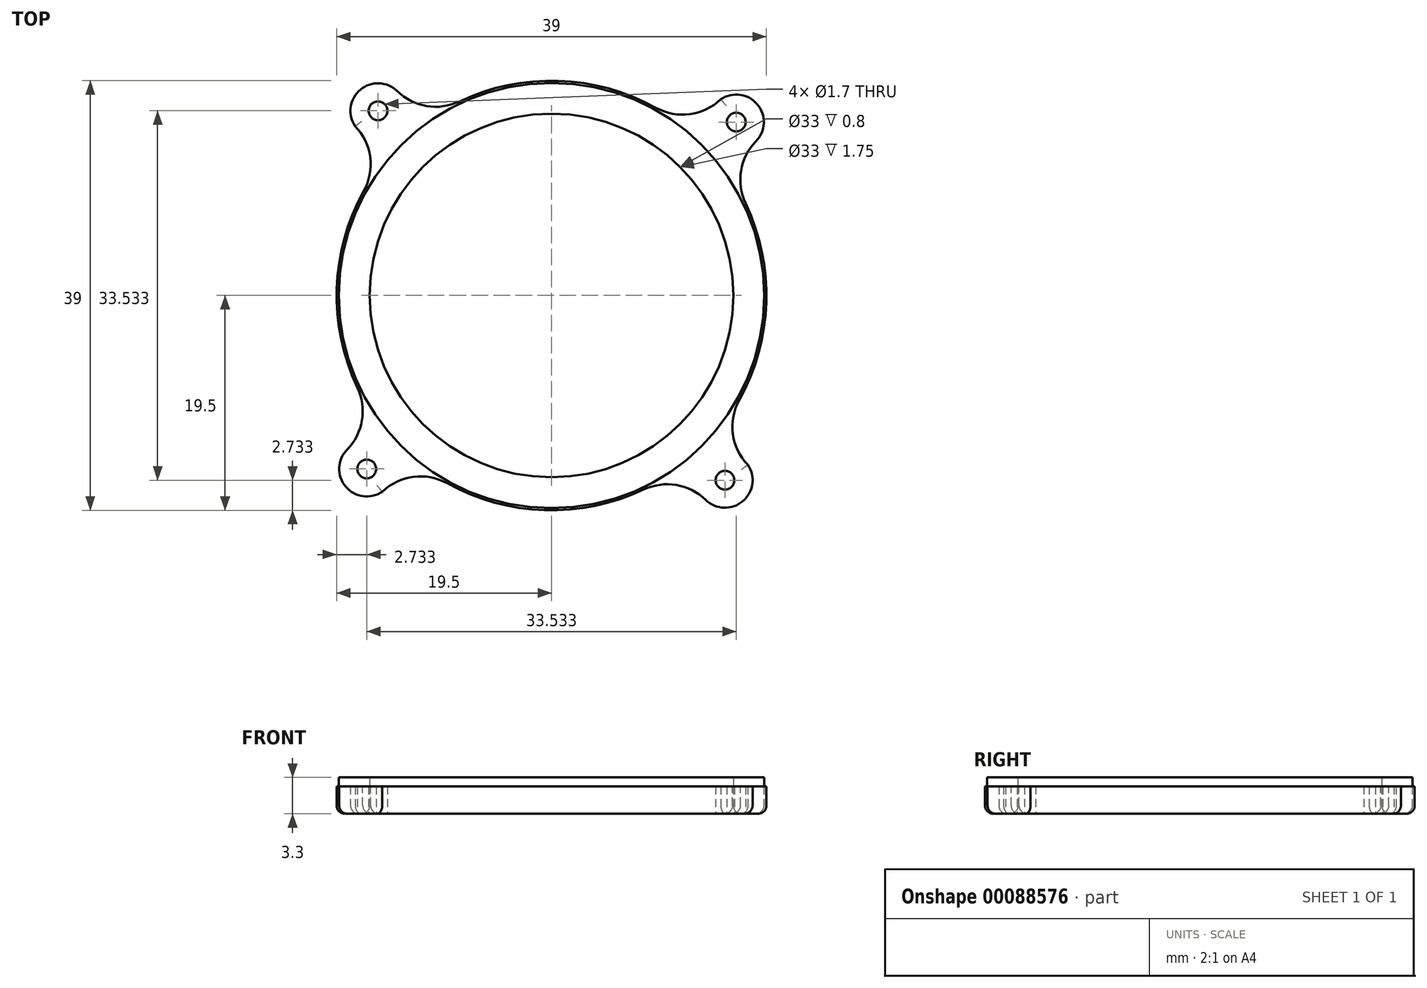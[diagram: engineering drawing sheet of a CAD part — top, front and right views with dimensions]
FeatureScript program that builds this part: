
annotation { "Feature Type Name" : "Feature", "Feature Type Description" : "" }
export const myFeature = defineFeature(function(context is Context, id is Id, definition is map)
    precondition{}
    {
        {
            var Q0;
            Q0=qCreatedBy(makeId("Top.planeOp"),FACE);
            var sketch = newSketch(context, id + "F0", { "sketchPlane" : qUnion([Q0])});
            skCircle(sketch, "E0", {"center": v(0, 0) * mm, "radius": 19.5 * mm});
            skCircle(sketch, "E1", {"center": v(0, 0) * mm, "radius": 16.5 * mm});
            skCircle(sketch, "E2", {"center": v(16.77, 15.74) * mm, "radius": 0.85 * mm});
            skCircle(sketch, "E3.1.0", {"center": v(-15.74, 16.77) * mm, "radius": 0.85 * mm});
            skCircle(sketch, "E3.2.0", {"center": v(-16.77, -15.74) * mm, "radius": 0.85 * mm});
            skCircle(sketch, "E3.3.0", {"center": v(15.74, -16.77) * mm, "radius": 0.85 * mm});
            skCircle(sketch, "E4", {"center": v(-15.74, 16.77) * mm, "radius": 2.5 * mm});
            skLineSegment(sketch, "E5", {"start": v(-13.87, 18.42) * mm, "end": v(-11.5, 15.75) * mm});
            skLineSegment(sketch, "E6", {"start": v(-17.81, 15.36) * mm, "end": v(-14.8, 12.7) * mm});
            skLineSegment(sketch, "E7.1.0", {"start": v(-18.42, -13.87) * mm, "end": v(-15.75, -11.5) * mm});
            skLineSegment(sketch, "E7.1.1", {"start": v(-15.36, -17.81) * mm, "end": v(-12.7, -14.8) * mm});
            skCircle(sketch, "E7.1.2", {"center": v(-16.77, -15.74) * mm, "radius": 2.5 * mm});
            skLineSegment(sketch, "E7.2.0", {"start": v(13.87, -18.42) * mm, "end": v(11.5, -15.75) * mm});
            skLineSegment(sketch, "E7.2.1", {"start": v(17.81, -15.36) * mm, "end": v(14.8, -12.7) * mm});
            skCircle(sketch, "E7.2.2", {"center": v(15.74, -16.77) * mm, "radius": 2.5 * mm});
            skLineSegment(sketch, "E7.3.0", {"start": v(18.42, 13.87) * mm, "end": v(15.75, 11.5) * mm});
            skLineSegment(sketch, "E7.3.1", {"start": v(15.36, 17.81) * mm, "end": v(12.7, 14.8) * mm});
            skCircle(sketch, "E7.3.2", {"center": v(16.77, 15.74) * mm, "radius": 2.5 * mm});
            skSolve(sketch);
        }
        {
            var Q0;
            Q0=makeQuery(id+"F0.imprint","IMPRINT",FACE,{"disambiguationData":[TD([[makeQuery(id+"F0.imprint","IMPRINT",EDGE,{"derivedFrom":sQuery(id+"F0.wireOp",EDGE,"E2")}),-1.0]])]});
            var Q1;
            {var subQ0=sQuery(id+"F0.wireOp",EDGE,"E7.3.0");Q1=makeQuery(id+"F0.imprint","IMPRINT",FACE,{"disambiguationData":[TD([[makeQuery(id+"F0.imprint","IMPRINT",EDGE,{"derivedFrom":subQ0}),-1.0]])]});}
            var Q2;
            Q2=makeQuery(id+"F0.imprint","IMPRINT",FACE,{"disambiguationData":[TD([[makeQuery(id+"F0.imprint","IMPRINT",EDGE,{"derivedFrom":sQuery(id+"F0.wireOp",EDGE,"E3.1.0")}),-1.0]])]});
            var Q3;
            {var subQ0=sQuery(id+"F0.wireOp",EDGE,"E5");Q3=makeQuery(id+"F0.imprint","IMPRINT",FACE,{"disambiguationData":[TD([[makeQuery(id+"F0.imprint","IMPRINT",EDGE,{"derivedFrom":subQ0}),-1.0]])]});}
            var Q4;
            Q4=makeQuery(id+"F0.imprint","IMPRINT",FACE,{"disambiguationData":[TD([[makeQuery(id+"F0.imprint","IMPRINT",EDGE,{"derivedFrom":sQuery(id+"F0.wireOp",EDGE,"E1")}),-1.0]])]});
            var Q5;
            {var subQ0=sQuery(id+"F0.wireOp",EDGE,"E7.2.0");Q5=makeQuery(id+"F0.imprint","IMPRINT",FACE,{"disambiguationData":[TD([[makeQuery(id+"F0.imprint","IMPRINT",EDGE,{"derivedFrom":subQ0}),-1.0]])]});}
            var Q6;
            {var subQ0=sQuery(id+"F0.wireOp",EDGE,"E7.1.0");Q6=makeQuery(id+"F0.imprint","IMPRINT",FACE,{"disambiguationData":[TD([[makeQuery(id+"F0.imprint","IMPRINT",EDGE,{"derivedFrom":subQ0}),-1.0]])]});}
            var Q7;
            Q7=makeQuery(id+"F0.imprint","IMPRINT",FACE,{"disambiguationData":[TD([[makeQuery(id+"F0.imprint","IMPRINT",EDGE,{"derivedFrom":sQuery(id+"F0.wireOp",EDGE,"E3.2.0")}),-1.0]])]});
            var Q8;
            Q8=makeQuery(id+"F0.imprint","IMPRINT",FACE,{"disambiguationData":[TD([[makeQuery(id+"F0.imprint","IMPRINT",EDGE,{"derivedFrom":sQuery(id+"F0.wireOp",EDGE,"E3.3.0")}),-1.0]])]});
            extrude(context, id + "F1", {"entities" : qUnion([Q0, Q1, Q2, Q3, Q4, Q5, Q6, Q7, Q8]), "depth" : 2.5 * mm});
        }
        {
            var Q0;
            Q0=makeQuery(id+"F1.opExtrude","SWEPT_EDGE",EDGE,{"disambiguationData":[OSD([sQuery(id+"F0.wireOp",EDGE,"E0"),sQuery(id+"F0.wireOp",EDGE,"E7.3.0")])]});
            var Q1;
            Q1=makeQuery(id+"F1.opExtrude","SWEPT_EDGE",EDGE,{"disambiguationData":[OSD([sQuery(id+"F0.wireOp",EDGE,"E0"),sQuery(id+"F0.wireOp",EDGE,"E7.3.1")])]});
            var Q2;
            Q2=makeQuery(id+"F1.opExtrude","SWEPT_EDGE",EDGE,{"disambiguationData":[OSD([sQuery(id+"F0.wireOp",EDGE,"E0"),sQuery(id+"F0.wireOp",EDGE,"E5")])]});
            var Q3;
            Q3=makeQuery(id+"F1.opExtrude","SWEPT_EDGE",EDGE,{"disambiguationData":[OSD([sQuery(id+"F0.wireOp",EDGE,"E0"),sQuery(id+"F0.wireOp",EDGE,"E6")])]});
            var Q4;
            Q4=makeQuery(id+"F1.opExtrude","SWEPT_EDGE",EDGE,{"disambiguationData":[OSD([sQuery(id+"F0.wireOp",EDGE,"E0"),sQuery(id+"F0.wireOp",EDGE,"E7.1.0")])]});
            var Q5;
            Q5=makeQuery(id+"F1.opExtrude","SWEPT_EDGE",EDGE,{"disambiguationData":[OSD([sQuery(id+"F0.wireOp",EDGE,"E0"),sQuery(id+"F0.wireOp",EDGE,"E7.1.1")])]});
            var Q6;
            Q6=makeQuery(id+"F1.opExtrude","SWEPT_EDGE",EDGE,{"disambiguationData":[OSD([sQuery(id+"F0.wireOp",EDGE,"E0"),sQuery(id+"F0.wireOp",EDGE,"E7.2.0")])]});
            var Q7;
            Q7=makeQuery(id+"F1.opExtrude","SWEPT_EDGE",EDGE,{"disambiguationData":[OSD([sQuery(id+"F0.wireOp",EDGE,"E0"),sQuery(id+"F0.wireOp",EDGE,"E7.2.1")])]});
            fillet(context, id + "F2", {"entities" : qUnion([Q0, Q1, Q2, Q3, Q4, Q5, Q6, Q7]), "radius" : 5 * mm, "tangentPropagation" : true, "allowEdgeOverflow" : false});
        }
        {
            var Q0;
            {var subQ0=sQuery(id+"F0.wireOp",EDGE,"E0");Q0=makeQuery(id+"F1.opExtrude","CAP_EDGE",EDGE,{"disambiguationData":[OSD([subQ0]),TDD([makeQuery(id+"F0.imprint","IMPRINT",EDGE,{"disambiguationData":[TD([[makeQuery(id+"F0.imprint","INTERSECT",VERTEX,{"derivedFrom":[subQ0,sQuery(id+"F0.wireOp",EDGE,"E6")]}),-1.0]])],"derivedFrom":subQ0})])],"isStart":true});}
            var Q1;
            {var subQ0=sQuery(id+"F0.wireOp",EDGE,"E6");var subQ1=sQuery(id+"F0.wireOp",EDGE,"E0");Q1=makeQuery(id+"F2.opFillet","BLEND_EDGE",EDGE,{"blendedFrom":[makeQuery(id+"F1.opExtrude","SWEPT_EDGE",EDGE,{"disambiguationData":[OSD([subQ1,subQ0])]}),makeQuery(id+"F1.opExtrude","CAP_FACE",FACE,{"disambiguationData":[OSD([subQ1,sQuery(id+"F0.wireOp",EDGE,"E1"),sQuery(id+"F0.wireOp",EDGE,"E2"),sQuery(id+"F0.wireOp",EDGE,"E3.1.0"),sQuery(id+"F0.wireOp",EDGE,"E3.2.0"),sQuery(id+"F0.wireOp",EDGE,"E3.3.0"),sQuery(id+"F0.wireOp",EDGE,"E4"),sQuery(id+"F0.wireOp",EDGE,"E5"),subQ0,sQuery(id+"F0.wireOp",EDGE,"E7.1.0"),sQuery(id+"F0.wireOp",EDGE,"E7.1.1"),sQuery(id+"F0.wireOp",EDGE,"E7.1.2"),sQuery(id+"F0.wireOp",EDGE,"E7.2.0"),sQuery(id+"F0.wireOp",EDGE,"E7.2.1"),sQuery(id+"F0.wireOp",EDGE,"E7.2.2"),sQuery(id+"F0.wireOp",EDGE,"E7.3.0"),sQuery(id+"F0.wireOp",EDGE,"E7.3.1"),sQuery(id+"F0.wireOp",EDGE,"E7.3.2")])],"isStart":true})],"blendedInto":[makeQuery(id+"F1.opExtrude","CAP_FACE",FACE,{"disambiguationData":[OSD([subQ1,sQuery(id+"F0.wireOp",EDGE,"E1"),sQuery(id+"F0.wireOp",EDGE,"E2"),sQuery(id+"F0.wireOp",EDGE,"E3.1.0"),sQuery(id+"F0.wireOp",EDGE,"E3.2.0"),sQuery(id+"F0.wireOp",EDGE,"E3.3.0"),sQuery(id+"F0.wireOp",EDGE,"E4"),sQuery(id+"F0.wireOp",EDGE,"E5"),subQ0,sQuery(id+"F0.wireOp",EDGE,"E7.1.0"),sQuery(id+"F0.wireOp",EDGE,"E7.1.1"),sQuery(id+"F0.wireOp",EDGE,"E7.1.2"),sQuery(id+"F0.wireOp",EDGE,"E7.2.0"),sQuery(id+"F0.wireOp",EDGE,"E7.2.1"),sQuery(id+"F0.wireOp",EDGE,"E7.2.2"),sQuery(id+"F0.wireOp",EDGE,"E7.3.0"),sQuery(id+"F0.wireOp",EDGE,"E7.3.1"),sQuery(id+"F0.wireOp",EDGE,"E7.3.2")])],"isStart":true})]});}
            var Q2;
            Q2=makeQuery(id+"F1.opExtrude","CAP_EDGE",EDGE,{"disambiguationData":[OSD([sQuery(id+"F0.wireOp",EDGE,"E4")])],"isStart":true});
            var Q3;
            {var subQ0=sQuery(id+"F0.wireOp",EDGE,"E5");var subQ1=sQuery(id+"F0.wireOp",EDGE,"E0");Q3=makeQuery(id+"F2.opFillet","BLEND_EDGE",EDGE,{"blendedFrom":[makeQuery(id+"F1.opExtrude","SWEPT_EDGE",EDGE,{"disambiguationData":[OSD([subQ1,subQ0])]}),makeQuery(id+"F1.opExtrude","CAP_FACE",FACE,{"disambiguationData":[OSD([subQ1,sQuery(id+"F0.wireOp",EDGE,"E1"),sQuery(id+"F0.wireOp",EDGE,"E2"),sQuery(id+"F0.wireOp",EDGE,"E3.1.0"),sQuery(id+"F0.wireOp",EDGE,"E3.2.0"),sQuery(id+"F0.wireOp",EDGE,"E3.3.0"),sQuery(id+"F0.wireOp",EDGE,"E4"),subQ0,sQuery(id+"F0.wireOp",EDGE,"E6"),sQuery(id+"F0.wireOp",EDGE,"E7.1.0"),sQuery(id+"F0.wireOp",EDGE,"E7.1.1"),sQuery(id+"F0.wireOp",EDGE,"E7.1.2"),sQuery(id+"F0.wireOp",EDGE,"E7.2.0"),sQuery(id+"F0.wireOp",EDGE,"E7.2.1"),sQuery(id+"F0.wireOp",EDGE,"E7.2.2"),sQuery(id+"F0.wireOp",EDGE,"E7.3.0"),sQuery(id+"F0.wireOp",EDGE,"E7.3.1"),sQuery(id+"F0.wireOp",EDGE,"E7.3.2")])],"isStart":true})],"blendedInto":[makeQuery(id+"F1.opExtrude","CAP_FACE",FACE,{"disambiguationData":[OSD([subQ1,sQuery(id+"F0.wireOp",EDGE,"E1"),sQuery(id+"F0.wireOp",EDGE,"E2"),sQuery(id+"F0.wireOp",EDGE,"E3.1.0"),sQuery(id+"F0.wireOp",EDGE,"E3.2.0"),sQuery(id+"F0.wireOp",EDGE,"E3.3.0"),sQuery(id+"F0.wireOp",EDGE,"E4"),subQ0,sQuery(id+"F0.wireOp",EDGE,"E6"),sQuery(id+"F0.wireOp",EDGE,"E7.1.0"),sQuery(id+"F0.wireOp",EDGE,"E7.1.1"),sQuery(id+"F0.wireOp",EDGE,"E7.1.2"),sQuery(id+"F0.wireOp",EDGE,"E7.2.0"),sQuery(id+"F0.wireOp",EDGE,"E7.2.1"),sQuery(id+"F0.wireOp",EDGE,"E7.2.2"),sQuery(id+"F0.wireOp",EDGE,"E7.3.0"),sQuery(id+"F0.wireOp",EDGE,"E7.3.1"),sQuery(id+"F0.wireOp",EDGE,"E7.3.2")])],"isStart":true})]});}
            var Q4;
            {var subQ0=sQuery(id+"F0.wireOp",EDGE,"E0");Q4=makeQuery(id+"F1.opExtrude","CAP_EDGE",EDGE,{"disambiguationData":[OSD([subQ0]),TDD([makeQuery(id+"F0.imprint","IMPRINT",EDGE,{"disambiguationData":[TD([[makeQuery(id+"F0.imprint","INTERSECT",VERTEX,{"derivedFrom":[subQ0,sQuery(id+"F0.wireOp",EDGE,"E5")]}),1.0]])],"derivedFrom":subQ0})])],"isStart":true});}
            var Q5;
            {var subQ0=sQuery(id+"F0.wireOp",EDGE,"E7.3.1");var subQ1=sQuery(id+"F0.wireOp",EDGE,"E0");Q5=makeQuery(id+"F2.opFillet","BLEND_EDGE",EDGE,{"blendedFrom":[makeQuery(id+"F1.opExtrude","SWEPT_EDGE",EDGE,{"disambiguationData":[OSD([subQ1,subQ0])]}),makeQuery(id+"F1.opExtrude","CAP_FACE",FACE,{"disambiguationData":[OSD([subQ1,sQuery(id+"F0.wireOp",EDGE,"E1"),sQuery(id+"F0.wireOp",EDGE,"E2"),sQuery(id+"F0.wireOp",EDGE,"E3.1.0"),sQuery(id+"F0.wireOp",EDGE,"E3.2.0"),sQuery(id+"F0.wireOp",EDGE,"E3.3.0"),sQuery(id+"F0.wireOp",EDGE,"E4"),sQuery(id+"F0.wireOp",EDGE,"E5"),sQuery(id+"F0.wireOp",EDGE,"E6"),sQuery(id+"F0.wireOp",EDGE,"E7.1.0"),sQuery(id+"F0.wireOp",EDGE,"E7.1.1"),sQuery(id+"F0.wireOp",EDGE,"E7.1.2"),sQuery(id+"F0.wireOp",EDGE,"E7.2.0"),sQuery(id+"F0.wireOp",EDGE,"E7.2.1"),sQuery(id+"F0.wireOp",EDGE,"E7.2.2"),sQuery(id+"F0.wireOp",EDGE,"E7.3.0"),subQ0,sQuery(id+"F0.wireOp",EDGE,"E7.3.2")])],"isStart":true})],"blendedInto":[makeQuery(id+"F1.opExtrude","CAP_FACE",FACE,{"disambiguationData":[OSD([subQ1,sQuery(id+"F0.wireOp",EDGE,"E1"),sQuery(id+"F0.wireOp",EDGE,"E2"),sQuery(id+"F0.wireOp",EDGE,"E3.1.0"),sQuery(id+"F0.wireOp",EDGE,"E3.2.0"),sQuery(id+"F0.wireOp",EDGE,"E3.3.0"),sQuery(id+"F0.wireOp",EDGE,"E4"),sQuery(id+"F0.wireOp",EDGE,"E5"),sQuery(id+"F0.wireOp",EDGE,"E6"),sQuery(id+"F0.wireOp",EDGE,"E7.1.0"),sQuery(id+"F0.wireOp",EDGE,"E7.1.1"),sQuery(id+"F0.wireOp",EDGE,"E7.1.2"),sQuery(id+"F0.wireOp",EDGE,"E7.2.0"),sQuery(id+"F0.wireOp",EDGE,"E7.2.1"),sQuery(id+"F0.wireOp",EDGE,"E7.2.2"),sQuery(id+"F0.wireOp",EDGE,"E7.3.0"),subQ0,sQuery(id+"F0.wireOp",EDGE,"E7.3.2")])],"isStart":true})]});}
            var Q6;
            Q6=makeQuery(id+"F1.opExtrude","CAP_EDGE",EDGE,{"disambiguationData":[OSD([sQuery(id+"F0.wireOp",EDGE,"E7.3.2")])],"isStart":true});
            var Q7;
            {var subQ0=sQuery(id+"F0.wireOp",EDGE,"E7.3.0");var subQ1=sQuery(id+"F0.wireOp",EDGE,"E0");Q7=makeQuery(id+"F2.opFillet","BLEND_EDGE",EDGE,{"blendedFrom":[makeQuery(id+"F1.opExtrude","SWEPT_EDGE",EDGE,{"disambiguationData":[OSD([subQ1,subQ0])]}),makeQuery(id+"F1.opExtrude","CAP_FACE",FACE,{"disambiguationData":[OSD([subQ1,sQuery(id+"F0.wireOp",EDGE,"E1"),sQuery(id+"F0.wireOp",EDGE,"E2"),sQuery(id+"F0.wireOp",EDGE,"E3.1.0"),sQuery(id+"F0.wireOp",EDGE,"E3.2.0"),sQuery(id+"F0.wireOp",EDGE,"E3.3.0"),sQuery(id+"F0.wireOp",EDGE,"E4"),sQuery(id+"F0.wireOp",EDGE,"E5"),sQuery(id+"F0.wireOp",EDGE,"E6"),sQuery(id+"F0.wireOp",EDGE,"E7.1.0"),sQuery(id+"F0.wireOp",EDGE,"E7.1.1"),sQuery(id+"F0.wireOp",EDGE,"E7.1.2"),sQuery(id+"F0.wireOp",EDGE,"E7.2.0"),sQuery(id+"F0.wireOp",EDGE,"E7.2.1"),sQuery(id+"F0.wireOp",EDGE,"E7.2.2"),subQ0,sQuery(id+"F0.wireOp",EDGE,"E7.3.1"),sQuery(id+"F0.wireOp",EDGE,"E7.3.2")])],"isStart":true})],"blendedInto":[makeQuery(id+"F1.opExtrude","CAP_FACE",FACE,{"disambiguationData":[OSD([subQ1,sQuery(id+"F0.wireOp",EDGE,"E1"),sQuery(id+"F0.wireOp",EDGE,"E2"),sQuery(id+"F0.wireOp",EDGE,"E3.1.0"),sQuery(id+"F0.wireOp",EDGE,"E3.2.0"),sQuery(id+"F0.wireOp",EDGE,"E3.3.0"),sQuery(id+"F0.wireOp",EDGE,"E4"),sQuery(id+"F0.wireOp",EDGE,"E5"),sQuery(id+"F0.wireOp",EDGE,"E6"),sQuery(id+"F0.wireOp",EDGE,"E7.1.0"),sQuery(id+"F0.wireOp",EDGE,"E7.1.1"),sQuery(id+"F0.wireOp",EDGE,"E7.1.2"),sQuery(id+"F0.wireOp",EDGE,"E7.2.0"),sQuery(id+"F0.wireOp",EDGE,"E7.2.1"),sQuery(id+"F0.wireOp",EDGE,"E7.2.2"),subQ0,sQuery(id+"F0.wireOp",EDGE,"E7.3.1"),sQuery(id+"F0.wireOp",EDGE,"E7.3.2")])],"isStart":true})]});}
            var Q8;
            {var subQ0=sQuery(id+"F0.wireOp",EDGE,"E0");Q8=makeQuery(id+"F1.opExtrude","CAP_EDGE",EDGE,{"disambiguationData":[OSD([subQ0]),TDD([makeQuery(id+"F0.imprint","IMPRINT",EDGE,{"disambiguationData":[TD([[makeQuery(id+"F0.imprint","INTERSECT",VERTEX,{"derivedFrom":[subQ0,sQuery(id+"F0.wireOp",EDGE,"E7.2.1")]}),-1.0]])],"derivedFrom":subQ0})])],"isStart":true});}
            var Q9;
            {var subQ0=sQuery(id+"F0.wireOp",EDGE,"E7.2.1");var subQ1=sQuery(id+"F0.wireOp",EDGE,"E0");Q9=makeQuery(id+"F2.opFillet","BLEND_EDGE",EDGE,{"blendedFrom":[makeQuery(id+"F1.opExtrude","SWEPT_EDGE",EDGE,{"disambiguationData":[OSD([subQ1,subQ0])]}),makeQuery(id+"F1.opExtrude","CAP_FACE",FACE,{"disambiguationData":[OSD([subQ1,sQuery(id+"F0.wireOp",EDGE,"E1"),sQuery(id+"F0.wireOp",EDGE,"E2"),sQuery(id+"F0.wireOp",EDGE,"E3.1.0"),sQuery(id+"F0.wireOp",EDGE,"E3.2.0"),sQuery(id+"F0.wireOp",EDGE,"E3.3.0"),sQuery(id+"F0.wireOp",EDGE,"E4"),sQuery(id+"F0.wireOp",EDGE,"E5"),sQuery(id+"F0.wireOp",EDGE,"E6"),sQuery(id+"F0.wireOp",EDGE,"E7.1.0"),sQuery(id+"F0.wireOp",EDGE,"E7.1.1"),sQuery(id+"F0.wireOp",EDGE,"E7.1.2"),sQuery(id+"F0.wireOp",EDGE,"E7.2.0"),subQ0,sQuery(id+"F0.wireOp",EDGE,"E7.2.2"),sQuery(id+"F0.wireOp",EDGE,"E7.3.0"),sQuery(id+"F0.wireOp",EDGE,"E7.3.1"),sQuery(id+"F0.wireOp",EDGE,"E7.3.2")])],"isStart":true})],"blendedInto":[makeQuery(id+"F1.opExtrude","CAP_FACE",FACE,{"disambiguationData":[OSD([subQ1,sQuery(id+"F0.wireOp",EDGE,"E1"),sQuery(id+"F0.wireOp",EDGE,"E2"),sQuery(id+"F0.wireOp",EDGE,"E3.1.0"),sQuery(id+"F0.wireOp",EDGE,"E3.2.0"),sQuery(id+"F0.wireOp",EDGE,"E3.3.0"),sQuery(id+"F0.wireOp",EDGE,"E4"),sQuery(id+"F0.wireOp",EDGE,"E5"),sQuery(id+"F0.wireOp",EDGE,"E6"),sQuery(id+"F0.wireOp",EDGE,"E7.1.0"),sQuery(id+"F0.wireOp",EDGE,"E7.1.1"),sQuery(id+"F0.wireOp",EDGE,"E7.1.2"),sQuery(id+"F0.wireOp",EDGE,"E7.2.0"),subQ0,sQuery(id+"F0.wireOp",EDGE,"E7.2.2"),sQuery(id+"F0.wireOp",EDGE,"E7.3.0"),sQuery(id+"F0.wireOp",EDGE,"E7.3.1"),sQuery(id+"F0.wireOp",EDGE,"E7.3.2")])],"isStart":true})]});}
            var Q10;
            Q10=makeQuery(id+"F1.opExtrude","CAP_EDGE",EDGE,{"disambiguationData":[OSD([sQuery(id+"F0.wireOp",EDGE,"E7.2.2")])],"isStart":true});
            var Q11;
            {var subQ0=sQuery(id+"F0.wireOp",EDGE,"E7.2.0");var subQ1=sQuery(id+"F0.wireOp",EDGE,"E0");Q11=makeQuery(id+"F2.opFillet","BLEND_EDGE",EDGE,{"blendedFrom":[makeQuery(id+"F1.opExtrude","SWEPT_EDGE",EDGE,{"disambiguationData":[OSD([subQ1,subQ0])]}),makeQuery(id+"F1.opExtrude","CAP_FACE",FACE,{"disambiguationData":[OSD([subQ1,sQuery(id+"F0.wireOp",EDGE,"E1"),sQuery(id+"F0.wireOp",EDGE,"E2"),sQuery(id+"F0.wireOp",EDGE,"E3.1.0"),sQuery(id+"F0.wireOp",EDGE,"E3.2.0"),sQuery(id+"F0.wireOp",EDGE,"E3.3.0"),sQuery(id+"F0.wireOp",EDGE,"E4"),sQuery(id+"F0.wireOp",EDGE,"E5"),sQuery(id+"F0.wireOp",EDGE,"E6"),sQuery(id+"F0.wireOp",EDGE,"E7.1.0"),sQuery(id+"F0.wireOp",EDGE,"E7.1.1"),sQuery(id+"F0.wireOp",EDGE,"E7.1.2"),subQ0,sQuery(id+"F0.wireOp",EDGE,"E7.2.1"),sQuery(id+"F0.wireOp",EDGE,"E7.2.2"),sQuery(id+"F0.wireOp",EDGE,"E7.3.0"),sQuery(id+"F0.wireOp",EDGE,"E7.3.1"),sQuery(id+"F0.wireOp",EDGE,"E7.3.2")])],"isStart":true})],"blendedInto":[makeQuery(id+"F1.opExtrude","CAP_FACE",FACE,{"disambiguationData":[OSD([subQ1,sQuery(id+"F0.wireOp",EDGE,"E1"),sQuery(id+"F0.wireOp",EDGE,"E2"),sQuery(id+"F0.wireOp",EDGE,"E3.1.0"),sQuery(id+"F0.wireOp",EDGE,"E3.2.0"),sQuery(id+"F0.wireOp",EDGE,"E3.3.0"),sQuery(id+"F0.wireOp",EDGE,"E4"),sQuery(id+"F0.wireOp",EDGE,"E5"),sQuery(id+"F0.wireOp",EDGE,"E6"),sQuery(id+"F0.wireOp",EDGE,"E7.1.0"),sQuery(id+"F0.wireOp",EDGE,"E7.1.1"),sQuery(id+"F0.wireOp",EDGE,"E7.1.2"),subQ0,sQuery(id+"F0.wireOp",EDGE,"E7.2.1"),sQuery(id+"F0.wireOp",EDGE,"E7.2.2"),sQuery(id+"F0.wireOp",EDGE,"E7.3.0"),sQuery(id+"F0.wireOp",EDGE,"E7.3.1"),sQuery(id+"F0.wireOp",EDGE,"E7.3.2")])],"isStart":true})]});}
            var Q12;
            Q12=makeQuery(id+"F1.opExtrude","CAP_EDGE",EDGE,{"disambiguationData":[OSD([sQuery(id+"F0.wireOp",EDGE,"E1")])],"isStart":true});
            fillet(context, id + "F3", {"entities" : qUnion([Q0, Q1, Q2, Q3, Q4, Q5, Q6, Q7, Q8, Q9, Q10, Q11, Q12]), "radius" : .75 * mm, "tangentPropagation" : true, "allowEdgeOverflow" : false});
        }
        {
            var Q0;
            Q0=makeQuery(id+"F1.opExtrude","CAP_FACE",FACE,{"disambiguationData":[OSD([sQuery(id+"F0.wireOp",EDGE,"E0"),sQuery(id+"F0.wireOp",EDGE,"E1"),sQuery(id+"F0.wireOp",EDGE,"E2"),sQuery(id+"F0.wireOp",EDGE,"E3.1.0"),sQuery(id+"F0.wireOp",EDGE,"E3.2.0"),sQuery(id+"F0.wireOp",EDGE,"E3.3.0"),sQuery(id+"F0.wireOp",EDGE,"E4"),sQuery(id+"F0.wireOp",EDGE,"E5"),sQuery(id+"F0.wireOp",EDGE,"E6"),sQuery(id+"F0.wireOp",EDGE,"E7.1.0"),sQuery(id+"F0.wireOp",EDGE,"E7.1.1"),sQuery(id+"F0.wireOp",EDGE,"E7.1.2"),sQuery(id+"F0.wireOp",EDGE,"E7.2.0"),sQuery(id+"F0.wireOp",EDGE,"E7.2.1"),sQuery(id+"F0.wireOp",EDGE,"E7.2.2"),sQuery(id+"F0.wireOp",EDGE,"E7.3.0"),sQuery(id+"F0.wireOp",EDGE,"E7.3.1"),sQuery(id+"F0.wireOp",EDGE,"E7.3.2")])],"isStart":false});
            var sketch = newSketch(context, id + "F4", { "sketchPlane" : qUnion([Q0])});
            skCircle(sketch, "E8", {"center": v(0, 0) * mm, "radius": 19.3 * mm});
            skCircle(sketch, "E9", {"center": v(0, 0) * mm, "radius": 16.5 * mm});
            skSolve(sketch);
        }
        {
            var Q0;
            Q0 = qSketchRegion(id + "F4", true);
            extrude(context, id + "F5", {"entities" : qUnion([Q0]), "depth" : .8 * mm});
        }
    });
